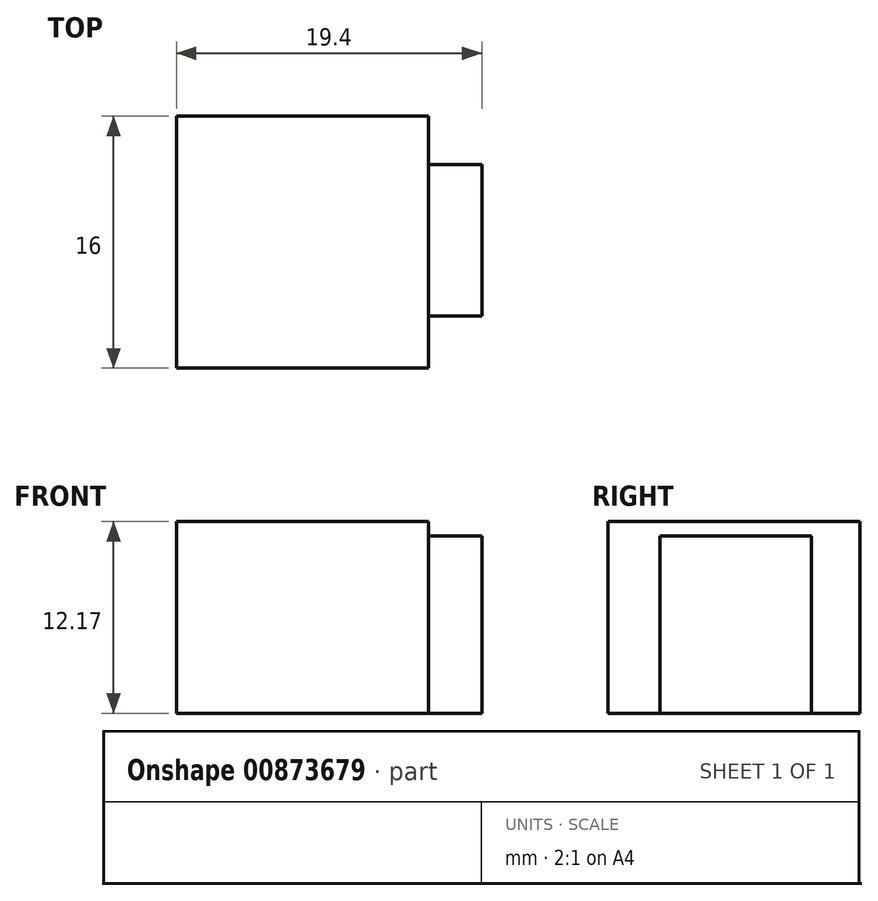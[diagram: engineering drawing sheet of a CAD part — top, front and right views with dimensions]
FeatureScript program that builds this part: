
annotation { "Feature Type Name" : "Feature", "Feature Type Description" : "" }
export const myFeature = defineFeature(function(context is Context, id is Id, definition is map)
    precondition{}
    {
        {
            var Q0;
            Q0=qCreatedBy(makeId("Top.planeOp"),FACE);
            var sketch = newSketch(context, id + "F0", { "sketchPlane" : qUnion([Q0])});
            skLineSegment(sketch, "E0.bottom", {"start": v(8, 8) * mm, "end": v(-8, 8) * mm});
            skLineSegment(sketch, "E0.top", {"start": v(8, -8) * mm, "end": v(-8, -8) * mm});
            skLineSegment(sketch, "E0.left", {"start": v(8, 8) * mm, "end": v(8, -8) * mm});
            skLineSegment(sketch, "E0.right", {"start": v(-8, 8) * mm, "end": v(-8, -8) * mm});
            skPoint(sketch, "E0.middle", {"position": v(0, 0) * mm});
            skSolve(sketch);
        }
        {
            var Q0;
            Q0=qSketchRegion(id+"F0",true);
            extrude(context, id + "F1", {"entities" : qUnion([Q0]), "depth" : 12.17 * mm, "offsetDistance" : 25 * mm});
        }
        {
            var Q0;
            Q0=makeQuery(id+"F1.opExtrude","SWEPT_FACE",FACE,{"disambiguationData":[OSD([sQuery(id+"F0.wireOp",EDGE,"E0.left")])]});
            var sketch = newSketch(context, id + "F2", { "sketchPlane" : qUnion([Q0])});
            skLineSegment(sketch, "E1.bottom", {"start": v(-4.7, 0) * mm, "end": v(4.94, 0) * mm});
            skLineSegment(sketch, "E1.top", {"start": v(-4.7, 11.25) * mm, "end": v(4.94, 11.25) * mm});
            skLineSegment(sketch, "E1.left", {"start": v(-4.7, 0) * mm, "end": v(-4.7, 11.25) * mm});
            skLineSegment(sketch, "E1.right", {"start": v(4.94, 0) * mm, "end": v(4.94, 11.25) * mm});
            skSolve(sketch);
        }
        {
            var Q0;
            Q0=qSketchRegion(id+"F2",true);
            extrude(context, id + "F3", {"entities" : qUnion([Q0]), "operationType" : NewBodyOperationType.ADD, "depth" : 3.4 * mm, "offsetDistance" : 25 * mm});
        }
    });
